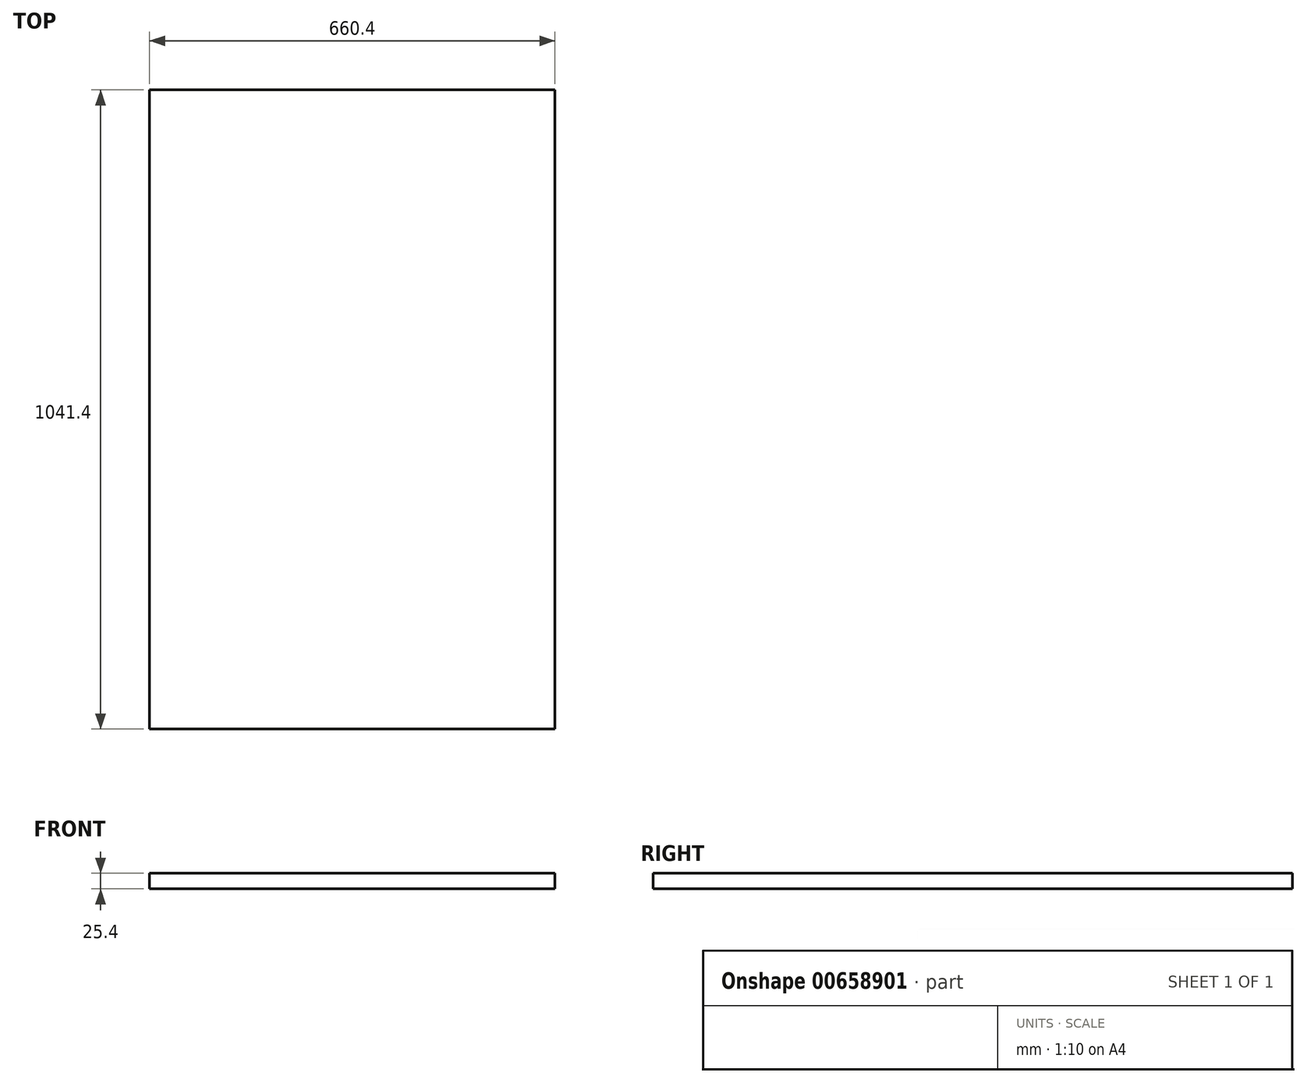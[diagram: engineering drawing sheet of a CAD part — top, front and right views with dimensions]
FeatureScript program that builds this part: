
annotation { "Feature Type Name" : "Feature", "Feature Type Description" : "" }
export const myFeature = defineFeature(function(context is Context, id is Id, definition is map)
    precondition{}
    {
        {
            var Q0;
            Q0=qCreatedBy(makeId("Top.planeOp"),FACE);
            var sketch = newSketch(context, id + "F0", { "sketchPlane" : qUnion([Q0])});
            skLineSegment(sketch, "E0.bottom", {"start": v(330.2, 520.7) * mm, "end": v(-330.2, 520.7) * mm});
            skLineSegment(sketch, "E0.top", {"start": v(330.2, -520.7) * mm, "end": v(-330.2, -520.7) * mm});
            skLineSegment(sketch, "E0.left", {"start": v(330.2, 520.7) * mm, "end": v(330.2, -520.7) * mm});
            skLineSegment(sketch, "E0.right", {"start": v(-330.2, 520.7) * mm, "end": v(-330.2, -520.7) * mm});
            skPoint(sketch, "E0.middle", {"position": v(0, 0) * mm});
            skSolve(sketch);
        }
        {
            var Q0;
            Q0=makeQuery(id+"F0.imprint","IMPRINT",FACE,{"disambiguationData":[TD([[makeQuery(id+"F0.imprint","IMPRINT",EDGE,{"derivedFrom":sQuery(id+"F0.wireOp",EDGE,"C3giivxW-MiYP-ZuVC-9Edc-9nVDn8w6Quuu")}),1.0]])]});
            var Q1;
            Q1=makeQuery(id+"F0.imprint","IMPRINT",FACE,{"disambiguationData":[TD([[makeQuery(id+"F0.imprint","IMPRINT",EDGE,{"derivedFrom":sQuery(id+"F0.wireOp",EDGE,"E0.bottom")}),1.0]])]});
            extrude(context, id + "F1", {"entities" : qUnion([Q0, Q1]), "depth" : 25.4 * mm, "offsetDistance" : 25.4 * mm});
        }
    });
